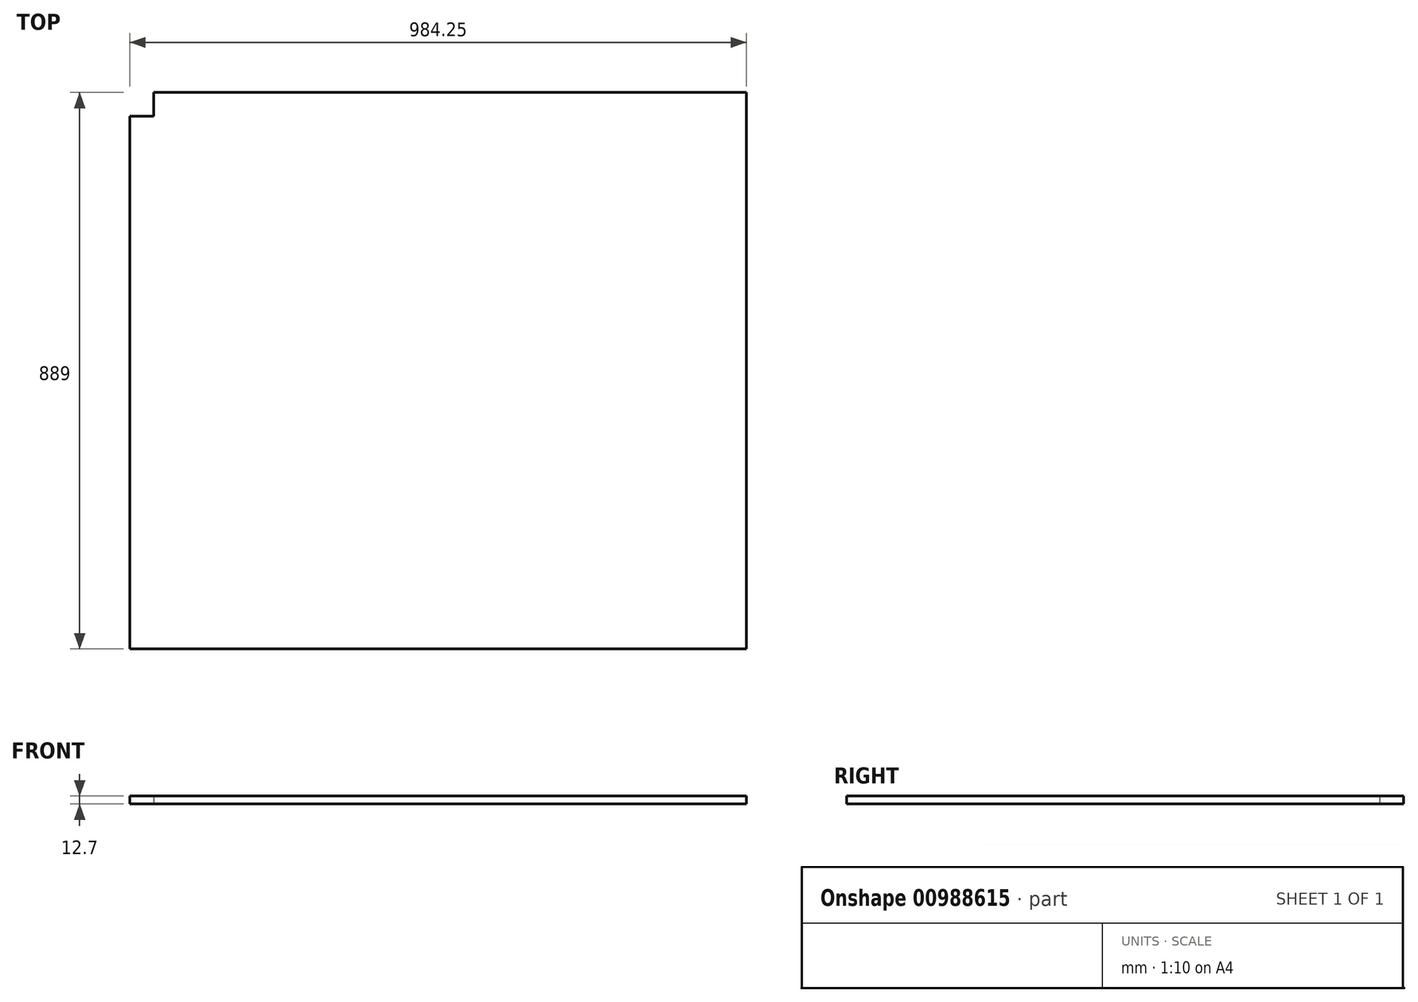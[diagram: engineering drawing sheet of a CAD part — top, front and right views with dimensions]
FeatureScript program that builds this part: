
annotation { "Feature Type Name" : "Feature", "Feature Type Description" : "" }
export const myFeature = defineFeature(function(context is Context, id is Id, definition is map)
    precondition{}
    {
        {
            var Q0;
            Q0=qCreatedBy(makeId("Top.planeOp"),FACE);
            var sketch = newSketch(context, id + "F0", { "sketchPlane" : qUnion([Q0])});
            skLineSegment(sketch, "E0.bottom", {"start": v(161.23, -412.28) * mm, "end": v(-543.62, -412.28) * mm});
            skLineSegment(sketch, "E0.top", {"start": v(161.23, -450.38) * mm, "end": v(-543.62, -450.38) * mm});
            skLineSegment(sketch, "E0.left", {"start": v(161.23, -412.28) * mm, "end": v(161.23, -450.38) * mm});
            skLineSegment(sketch, "E0.right", {"start": v(-543.62, -412.28) * mm, "end": v(-543.62, -450.38) * mm});
            skPoint(sketch, "E0.middle", {"position": v(-191.2, -431.33) * mm});
            skLineSegment(sketch, "E1.bottom", {"start": v(-543.62, -450.38) * mm, "end": v(-488.67, -450.38) * mm});
            skLineSegment(sketch, "E2.bottom", {"start": v(-543.62, -450.38) * mm, "end": v(-505.52, -450.38) * mm});
            skLineSegment(sketch, "E2.top", {"start": v(-543.62, 438.62) * mm, "end": v(-505.52, 438.62) * mm});
            skLineSegment(sketch, "E2.left", {"start": v(-543.62, -450.38) * mm, "end": v(-543.62, 438.62) * mm});
            skLineSegment(sketch, "E2.right", {"start": v(-505.52, -450.38) * mm, "end": v(-505.52, 438.62) * mm});
            skLineSegment(sketch, "E3.bottom", {"start": v(161.23, -450.38) * mm, "end": v(123.13, -450.38) * mm});
            skLineSegment(sketch, "E3.top", {"start": v(161.23, 438.62) * mm, "end": v(123.13, 438.62) * mm});
            skLineSegment(sketch, "E3.left", {"start": v(161.23, -450.38) * mm, "end": v(161.23, 438.62) * mm});
            skLineSegment(sketch, "E3.right", {"start": v(123.13, -450.38) * mm, "end": v(123.13, 438.62) * mm});
            skLineSegment(sketch, "E4.bottom", {"start": v(161.23, 438.62) * mm, "end": v(-543.62, 438.62) * mm});
            skLineSegment(sketch, "E4.top", {"start": v(161.23, 400.52) * mm, "end": v(-543.62, 400.52) * mm});
            skLineSegment(sketch, "E4.left", {"start": v(161.23, 438.62) * mm, "end": v(161.23, 400.52) * mm});
            skLineSegment(sketch, "E4.right", {"start": v(-543.62, 438.62) * mm, "end": v(-543.62, 400.52) * mm});
            skLineSegment(sketch, "E5.bottom", {"start": v(161.23, 438.62) * mm, "end": v(161.23, 438.62) * mm});
            skLineSegment(sketch, "E5.top", {"start": v(161.23, 400.52) * mm, "end": v(161.23, 400.52) * mm});
            skLineSegment(sketch, "E6.left", {"start": v(161.23, 438.62) * mm, "end": v(161.23, 399.43) * mm});
            skLineSegment(sketch, "E7.left", {"start": v(161.23, -450.38) * mm, "end": v(161.23, -412.28) * mm});
            skLineSegment(sketch, "E8.bottom", {"start": v(161.23, -450.38) * mm, "end": v(440.63, -450.38) * mm});
            skLineSegment(sketch, "E8.top", {"start": v(161.23, 438.62) * mm, "end": v(440.63, 438.62) * mm});
            skLineSegment(sketch, "E8.right", {"start": v(440.63, -450.38) * mm, "end": v(440.63, 438.62) * mm});
            skSolve(sketch);
        }
        {
            var Q0;
            {var subQ3=sQuery(id+"F0.wireOp",EDGE,"E8.bottom");Q0=makeQuery(id+"F0.imprint","IMPRINT",FACE,{"disambiguationData":[TD([[makeQuery(id+"F0.imprint","IMPRINT",EDGE,{"derivedFrom":subQ3}),1.0]])]});}
            var Q1;
            {var subQ0=sQuery(id+"F0.wireOp",EDGE,"E4.bottom");var subQ1=sQuery(id+"F0.wireOp",EDGE,"E3.right");var subQ2=makeQuery(id+"F0.imprint","INTERSECT",VERTEX,{"derivedFrom":[subQ1,subQ0]});Q1=makeQuery(id+"F0.imprint","IMPRINT",FACE,{"disambiguationData":[TD([[makeQuery(id+"F0.imprint","IMPRINT",EDGE,{"disambiguationData":[TD([[subQ2,1.0]])],"derivedFrom":subQ1}),-1.0]])]});}
            var Q2;
            {var subQ0=sQuery(id+"F0.wireOp",EDGE,"E3.left");var subQ8=makeQuery(id+"F0.imprint","IMPRINT",VERTEX,{"derivedFrom":subQ0});Q2=makeQuery(id+"F0.imprint","IMPRINT",FACE,{"disambiguationData":[TD([[makeQuery(id+"F0.imprint","IMPRINT",EDGE,{"disambiguationData":[TD([[subQ8,1.0]])],"derivedFrom":subQ0}),1.0]])]});}
            var Q3;
            {var subQ5=sQuery(id+"F0.wireOp",EDGE,"E3.bottom");Q3=makeQuery(id+"F0.imprint","IMPRINT",FACE,{"disambiguationData":[TD([[makeQuery(id+"F0.imprint","IMPRINT",EDGE,{"derivedFrom":subQ5}),-1.0]])]});}
            var Q4;
            {var subQ4=sQuery(id+"F0.wireOp",EDGE,"E0.top");Q4=makeQuery(id+"F0.imprint","IMPRINT",FACE,{"disambiguationData":[TD([[makeQuery(id+"F0.imprint","IMPRINT",EDGE,{"derivedFrom":subQ4}),-1.0]])]});}
            var Q5;
            {var subQ0=sQuery(id+"F0.wireOp",EDGE,"E3.right");var subQ1=sQuery(id+"F0.wireOp",EDGE,"E0.bottom");var subQ2=makeQuery(id+"F0.imprint","INTERSECT",VERTEX,{"derivedFrom":[subQ1,subQ0]});Q5=makeQuery(id+"F0.imprint","IMPRINT",FACE,{"disambiguationData":[TD([[makeQuery(id+"F0.imprint","IMPRINT",EDGE,{"disambiguationData":[TD([[subQ2,-1.0]])],"derivedFrom":subQ1}),-1.0]])]});}
            var Q6;
            {var subQ0=sQuery(id+"F0.wireOp",EDGE,"E4.bottom");var subQ1=sQuery(id+"F0.wireOp",EDGE,"E2.right");var subQ2=makeQuery(id+"F0.imprint","INTERSECT",VERTEX,{"derivedFrom":[subQ1,subQ0]});Q6=makeQuery(id+"F0.imprint","IMPRINT",FACE,{"disambiguationData":[TD([[makeQuery(id+"F0.imprint","IMPRINT",EDGE,{"disambiguationData":[TD([[subQ2,1.0]])],"derivedFrom":subQ1}),-1.0]])]});}
            var Q7;
            {var subQ5=sQuery(id+"F0.wireOp",EDGE,"E4.right");Q7=makeQuery(id+"F0.imprint","IMPRINT",FACE,{"disambiguationData":[TD([[makeQuery(id+"F0.imprint","IMPRINT",EDGE,{"derivedFrom":subQ5}),1.0]])]});}
            var Q8;
            {var subQ0=sQuery(id+"F0.wireOp",EDGE,"E2.left");var subQ1=sQuery(id+"F0.wireOp",EDGE,"E0.bottom");var subQ2=makeQuery(id+"F0.imprint","INTERSECT",VERTEX,{"derivedFrom":[subQ1,subQ0]});Q8=makeQuery(id+"F0.imprint","IMPRINT",FACE,{"disambiguationData":[TD([[makeQuery(id+"F0.imprint","IMPRINT",EDGE,{"disambiguationData":[TD([[subQ2,1.0]])],"derivedFrom":subQ1}),-1.0]])]});}
            var Q9;
            {var subQ5=sQuery(id+"F0.wireOp",EDGE,"E2.bottom");Q9=makeQuery(id+"F0.imprint","IMPRINT",FACE,{"disambiguationData":[TD([[makeQuery(id+"F0.imprint","IMPRINT",EDGE,{"derivedFrom":subQ5}),1.0]])]});}
            extrude(context, id + "F1", {"entities" : qUnion([Q0, Q1, Q2, Q3, Q4, Q5, Q6, Q7, Q8, Q9]), "depth" : 12.7 * mm, "offsetDistance" : 25.4 * mm});
        }
    });
